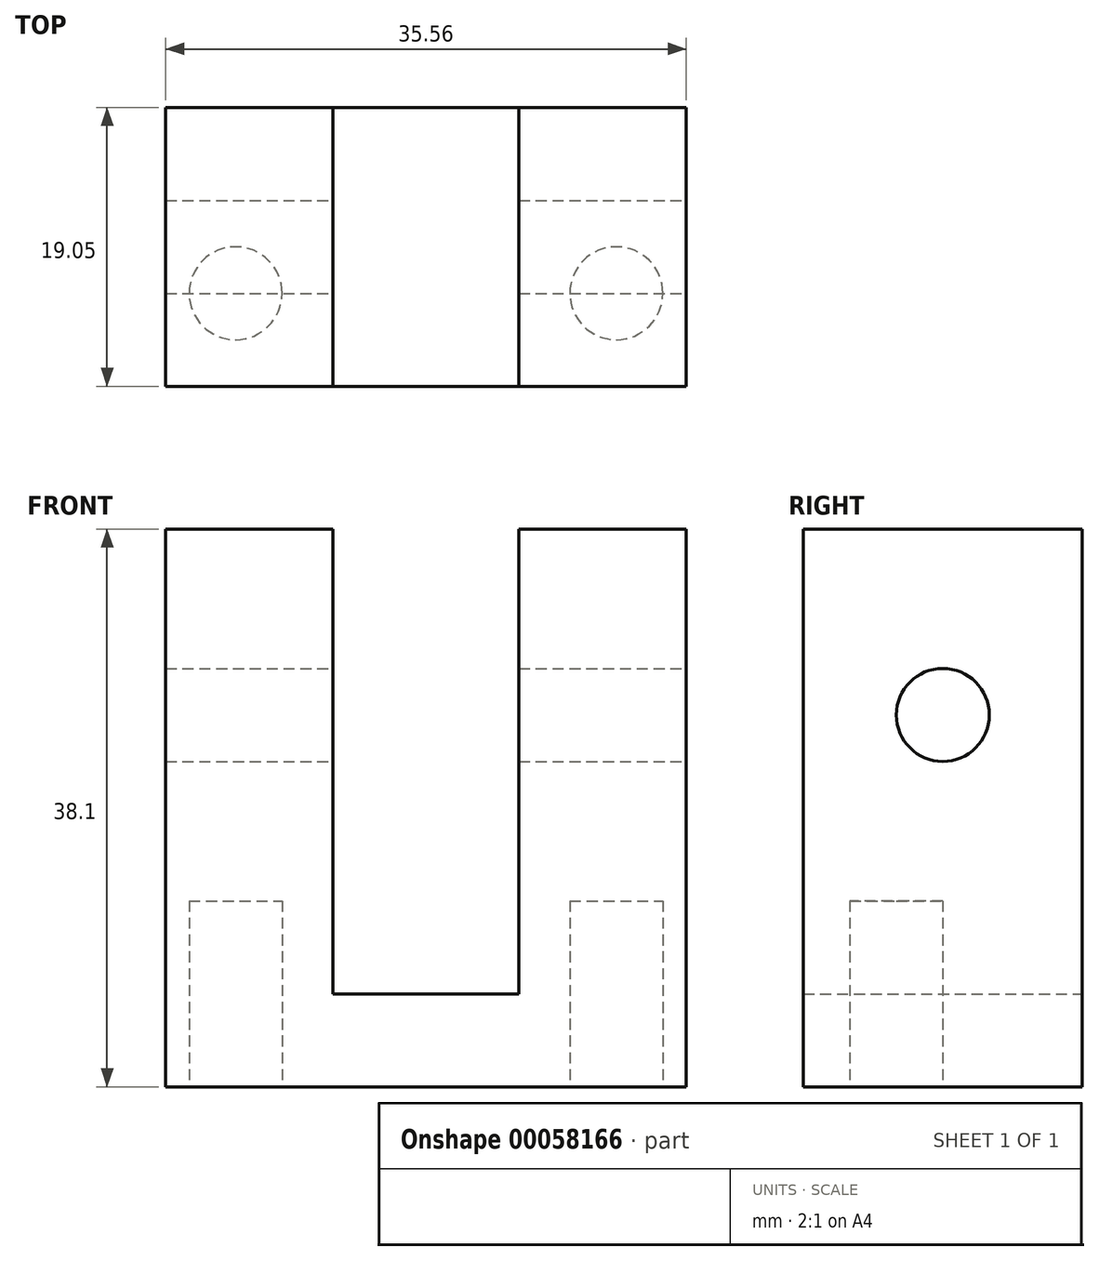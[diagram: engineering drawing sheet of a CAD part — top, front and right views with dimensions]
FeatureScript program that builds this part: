
annotation { "Feature Type Name" : "Feature", "Feature Type Description" : "" }
export const myFeature = defineFeature(function(context is Context, id is Id, definition is map)
    precondition{}
    {
        {
            var Q0;
            Q0=qCreatedBy(makeId("Front.planeOp"),FACE);
            var sketch = newSketch(context, id + "F0", { "sketchPlane" : qUnion([Q0])});
            skLineSegment(sketch, "E0", {"start": v(0, 0) * mm, "end": v(0, 38.1) * mm});
            skLineSegment(sketch, "E1", {"start": v(0, 38.1) * mm, "end": v(11.43, 38.1) * mm});
            skLineSegment(sketch, "E2", {"start": v(11.43, 38.1) * mm, "end": v(11.43, 6.35) * mm});
            skLineSegment(sketch, "E3", {"start": v(11.43, 6.35) * mm, "end": v(24.13, 6.35) * mm});
            skLineSegment(sketch, "E4", {"start": v(24.13, 6.35) * mm, "end": v(24.13, 38.1) * mm});
            skLineSegment(sketch, "E5", {"start": v(24.13, 38.1) * mm, "end": v(35.56, 38.1) * mm});
            skLineSegment(sketch, "E6", {"start": v(35.56, 38.1) * mm, "end": v(35.56, 0) * mm});
            skLineSegment(sketch, "E7", {"start": v(35.56, 0) * mm, "end": v(0, 0) * mm});
            skSolve(sketch);
        }
        {
            var Q0;
            Q0=makeQuery(id+"F0.imprint","IMPRINT",FACE,{"disambiguationData":[TD([[makeQuery(id+"F0.imprint","IMPRINT",EDGE,{"derivedFrom":sQuery(id+"F0.wireOp",EDGE,"E0")}),-1.0]])]});
            extrude(context, id + "F1", {"entities" : qUnion([Q0]), "depth" : 19.05 * mm});
        }
        {
            var Q0;
            Q0=makeQuery(id+"F1.opExtrude","SWEPT_FACE",FACE,{"disambiguationData":[OSD([sQuery(id+"F0.wireOp",EDGE,"E6")])]});
            var sketch = newSketch(context, id + "F2", { "sketchPlane" : qUnion([Q0])});
            skCircle(sketch, "E8", {"center": v(-9.53, 25.4) * mm, "radius": 3.18 * mm});
            skSolve(sketch);
        }
        {
            var Q0;
            Q0=makeQuery(id+"F2.imprint","IMPRINT",FACE,{"disambiguationData":[TD([[makeQuery(id+"F2.imprint","IMPRINT",EDGE,{"derivedFrom":sQuery(id+"F2.wireOp",EDGE,"E8")}),1.0]])]});
            extrude(context, id + "F3", {"entities" : qUnion([Q0]), "operationType" : NewBodyOperationType.REMOVE, "endBound" : BoundingType.THROUGH_ALL, "oppositeDirection" : true, "depth" : 25.4 * mm});
        }
        {
            var Q0;
            Q0=makeQuery(id+"F1.opExtrude","SWEPT_FACE",FACE,{"disambiguationData":[OSD([sQuery(id+"F0.wireOp",EDGE,"E7")])]});
            var sketch = newSketch(context, id + "F4", { "sketchPlane" : qUnion([Q0])});
            skCircle(sketch, "E9", {"center": v(4.78, 12.7) * mm, "radius": 3.18 * mm});
            skCircle(sketch, "E10", {"center": v(30.78, 12.7) * mm, "radius": 3.18 * mm});
            skSolve(sketch);
        }
        {
            var Q0;
            Q0=makeQuery(id+"F4.imprint","IMPRINT",FACE,{"disambiguationData":[TD([[makeQuery(id+"F4.imprint","IMPRINT",EDGE,{"derivedFrom":sQuery(id+"F4.wireOp",EDGE,"E9")}),1.0]])]});
            var Q1;
            Q1=makeQuery(id+"F4.imprint","IMPRINT",FACE,{"disambiguationData":[TD([[makeQuery(id+"F4.imprint","IMPRINT",EDGE,{"derivedFrom":sQuery(id+"F4.wireOp",EDGE,"E10")}),1.0]])]});
            extrude(context, id + "F5", {"entities" : qUnion([Q0, Q1]), "operationType" : NewBodyOperationType.REMOVE, "oppositeDirection" : true, "depth" : 12.7 * mm});
        }
    });
